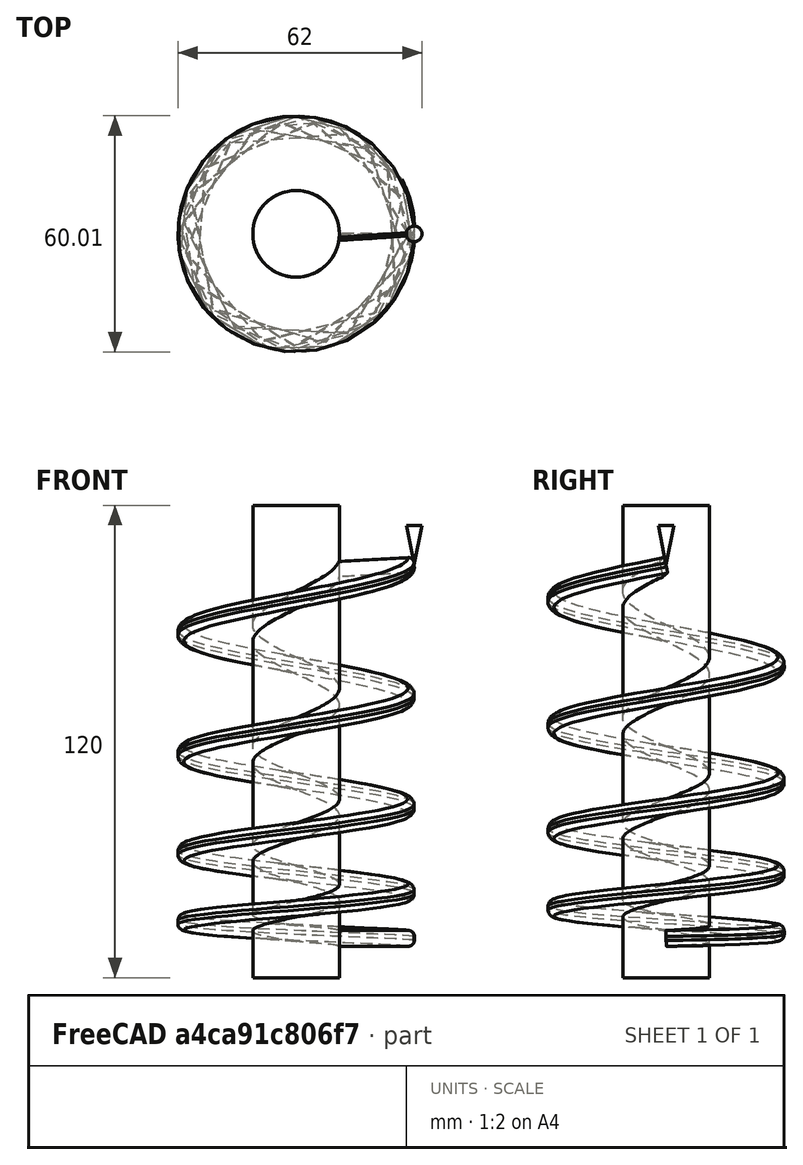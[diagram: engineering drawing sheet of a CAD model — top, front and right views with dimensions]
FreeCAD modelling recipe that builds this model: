
FCSTD DOCUMENT  (FreeCAD 0.18.2R)
Label: WORM SCREW
License: All rights reserved
LicenseURL: http://en.wikipedia.org/wiki/All_rights_reserved
objects: App::FeaturePython×4, App::DocumentObjectGroupPython×2, Part::Cone×1, Part::Part2DObjectPython×1, Part::Plane×1, Part::Sweep×1, Part::Fillet×1, Part::Cylinder×1, Part::MultiFuse×1
note: 7 computed .brp shape members not serialized (recipe doc carries the construction recipe); baked Part::Feature solids carry a one-line shape summary decoded from their .brp

FEATURE [Part::Cone] Cone
  Angle = 360
  AttacherType = Attacher::AttachEngine3D
  Height = 10
  Placement = pos=(30,-2.94e-14,94.8683) rot=(0,0,1;0rad)
  Radius1 = 0
  Radius2 = 2
FEATURE [App::DocumentObjectGroupPython] My_Placer  # scripted group (container) (typed FeaturePython)
  Placement = pos=(30,-2.94e-14,94.8683) rot=(0,0,1;0rad)
  RotAxis = (0,0,1)
  RotCenter = (0,0,0)
  arc = 0
  arc0 = 0
  arc1 = 90
  target = -> Cone
  time = 1
  x = x0
  x0 = 30
  x1 = 200
  y = y0
  y0 = -2.94e-14
  y1 = 10
  z = z0
  z0 = 94.8683
  z1 = 0
  expr: z0 = 3 * y1 ^ 1.5
  expr: y1 = time * 10
  expr: y0 = 30 * sin(time * 360 * 4)
  expr: x0 = 30 * cos(time * 360 * 4)
FEATURE [App::DocumentObjectGroupPython] My_Manager  # scripted group (container) (typed FeaturePython)
  Group = -> [My_Placer]
  intervall = 100
  sleeptime = 0.02
  start = 0
  step = 100
  text = NO
FEATURE [Part::Part2DObjectPython] BSpline  # Draft 2D object (typed FeaturePython)
  Closed = false
  MakeFace = true
  Parameterization = 1
  Points = (35) [(30,0,0),(21.8691,20.5364,0.49295),(1.88372,29.9408,1.39427),(-19.1227,23.1154,2.56144),(-29.7634,3.76,3.9436),(-24.2705,-17.6336,5.51135),+29 more]
FEATURE [Part::Plane] Plane
  AttacherType = Attacher::AttachEngine3D
  Length = 20
  Placement = pos=(10,-0.00946566,2.0015) rot=(-1,0,0;1.53589rad)
  Width = 4
FEATURE [Part::Sweep] Sweep
  Frenet = true
  Sections = -> [Plane]
  Solid = true
  Spine = -> BSpline [Edge1]
  Transition = 1
FEATURE [Part::Fillet] Fillet
  Base = -> Sweep
  Edges = 2 edges r=1.5: [Edge6,Edge9]
FEATURE [Part::Cylinder] Cylinder
  Angle = 360
  AttacherType = Attacher::AttachEngine3D
  Height = 120
  Placement = pos=(0,0,-10) rot=(0,0,1;0rad)
  Radius = 11
FEATURE [Part::MultiFuse] Fusion
  Shapes = -> [Fillet,Cylinder]
FEATURE [App::FeaturePython] Dimension  # Draft dimension (typed FeaturePython)
  Diameter = false
  Dimline = (36.3584,0,12.0235)
  Direction = (0,0,0)
  Distance = 12.1039
  End = (29.6083,3.70476,0.0538523)
  Normal = (0,-1,0)
  Start = (29.7525,2.49714,12.0965)
FEATURE [App::FeaturePython] Dimension001  # Draft dimension (typed FeaturePython)
  Diameter = false
  Dimline = (36.328,0.254405,9.48655)
  Direction = (0,0,0)
  Distance = 21.552
  End = (29.714,1.49973,12.0022)
  Normal = (0,-1,0)
  Start = (29.8772,-0.984422,33.4099)
FEATURE [App::FeaturePython] Dimension002  # Draft dimension (typed FeaturePython)
  Diameter = false
  Dimline = (36.4876,-2.17474,30.4202)
  Direction = (0,0,0)
  Distance = 28.3262
  End = (29.9793,-1.00769,33.4064)
  Normal = (0,-1,0)
  Start = (29.9584,0.462993,61.6944)
FEATURE [App::FeaturePython] Dimension003  # Draft dimension (typed FeaturePython)
  Diameter = false
  Dimline = (36.467,-0.729752,58.2138)
  Direction = (0,0,0)
  Distance = 33.1772
  End = (29.9584,0.462993,61.6944)
  Normal = (0,-1,0)
  Start = (30,-2.94e-14,94.8683)
